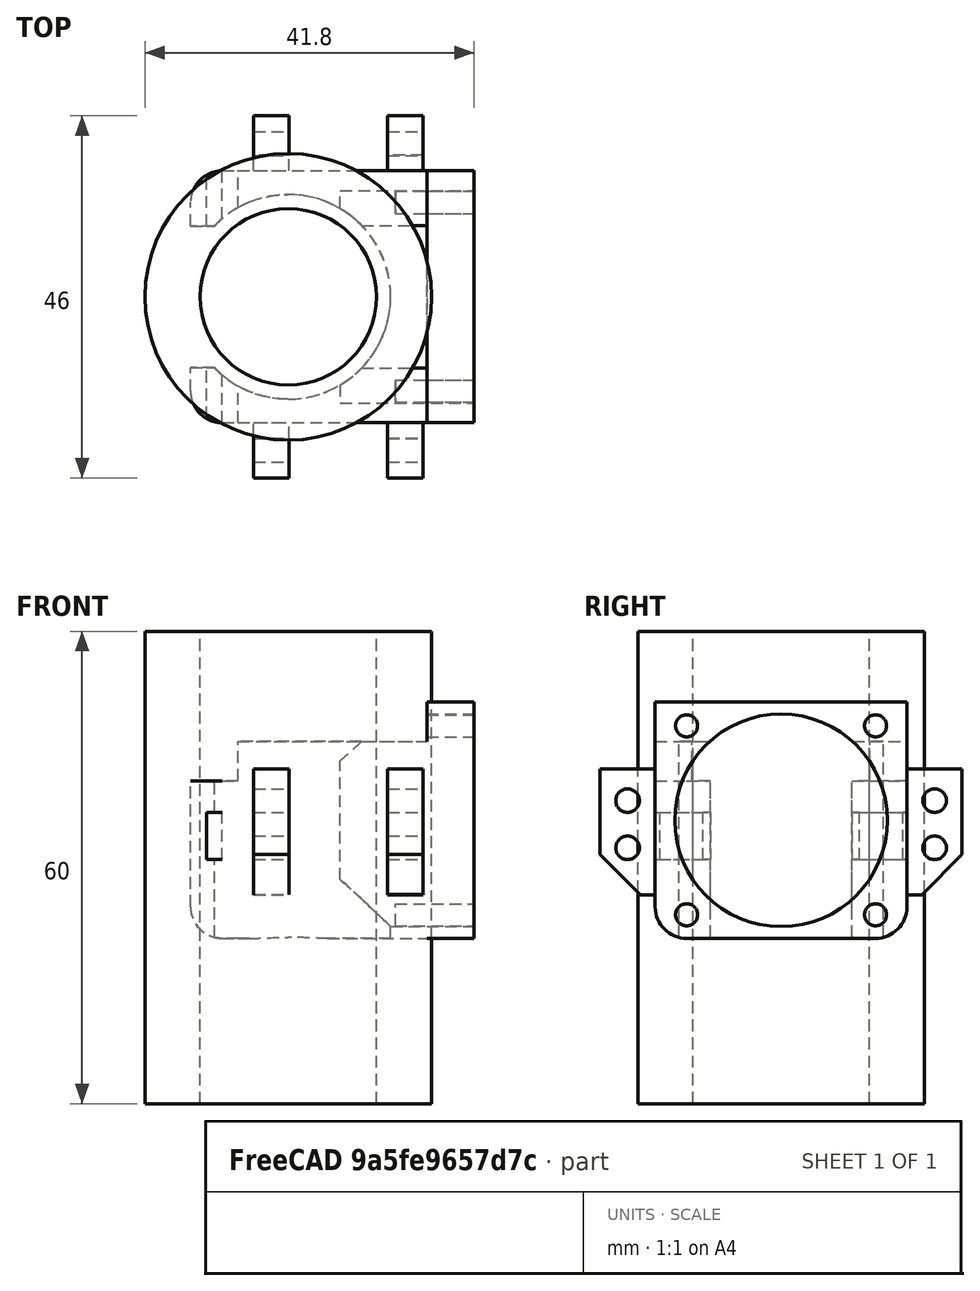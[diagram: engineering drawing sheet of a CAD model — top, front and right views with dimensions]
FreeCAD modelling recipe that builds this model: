
FCSTD DOCUMENT  (FreeCAD 0.15R4671 (Git))
Label: e3dv5
License: All rights reserved
LicenseURL: http://en.wikipedia.org/wiki/All_rights_reserved
objects: Part::Box×13, Part::Cylinder×12, Part::MultiFuse×6, Part::Fillet×4, Part::Cut×3, Mesh::Feature×2, Part::Feature×2
note: 40 computed .brp shape members not serialized (recipe doc carries the construction recipe); baked Part::Feature solids carry a one-line shape summary decoded from their .brp

FEATURE [Part::Box] Box  label="CubeMain"
  Height = 25
  Length = 24
  Width = 32
FEATURE [Part::Box] Box001  label="CubeFrontMask"
  Height = 30
  Length = 6
  Placement = pos=(24,0,0) rot=(0,0,1;0rad)
  Width = 32
FEATURE [Part::Cylinder] Cylinder  label="CylinderHeatSink"
  Angle = 360
  Height = 25
  Placement = pos=(6.4,16,0) rot=(0,0,1;0rad)
  Radius = 13
FEATURE [Part::Cylinder] Cylinder001  label="CylinderFan"
  Angle = 360
  Height = 18
  Placement = pos=(13,16,15) rot=(0,1,0;1.5708rad)
  Radius = 13.5
FEATURE [Part::Cylinder] Cylinder002  label="CylinderBL"
  Angle = 360
  Height = 20
  Placement = pos=(20,4,3) rot=(0,1,0;1.5708rad)
  Radius = 1.4
FEATURE [Part::Cylinder] Cylinder003  label="CylinderTL"
  Angle = 360
  Height = 20
  Placement = pos=(20,4,27) rot=(0,1,0;1.5708rad)
  Radius = 1.4
FEATURE [Part::Cylinder] Cylinder004  label="CylinderTB"
  Angle = 360
  Height = 20
  Placement = pos=(20,28,27) rot=(0,1,0;1.5708rad)
  Radius = 1.4
FEATURE [Part::Cylinder] Cylinder005  label="CylinderRB"
  Angle = 360
  Height = 20
  Placement = pos=(20,28,3) rot=(0,1,0;1.5708rad)
  Radius = 1.4
FEATURE [Part::MultiFuse] Fusion001  label="FusionFanScrews"
  Shapes = -> [Cylinder002,Cylinder003,Cylinder005,Cylinder004]
FEATURE [Part::Box] Box002  label="CubeZipTieL"
  Height = 20
  Length = 6
  Placement = pos=(-6,0,0) rot=(0,0,1;0rad)
  Width = 7
FEATURE [Part::Box] Box003  label="CubZipTieR"
  Height = 20
  Length = 6
  Placement = pos=(-6,25,0) rot=(0,0,1;0rad)
  Width = 7
FEATURE [Part::Box] Box004  label="CubeZipTieHor"
  Height = 6
  Length = 2
  Placement = pos=(-4,0,10) rot=(0,0,1;0rad)
  Width = 32
FEATURE [Part::Cylinder] Cylinder009
  Angle = 360
  Height = 40
  Placement = pos=(0,-3.5,12) rot=(0,1,0;1.5708rad)
  Radius = 1.5
FEATURE [Part::Cylinder] Cylinder010
  Angle = 360
  Height = 40
  Placement = pos=(0,-3.5,6) rot=(0,1,0;1.5708rad)
  Radius = 1.5
FEATURE [Part::Box] Box005  label="Cube005"
  Height = 16
  Length = 4.5
  Placement = pos=(2,-7,0) rot=(0,0,1;0rad)
  Width = 7
FEATURE [Part::Box] Box006  label="Cube006"
  Height = 16
  Length = 4.5
  Placement = pos=(19,-7,0) rot=(0,0,1;0rad)
  Width = 7
FEATURE [Part::Box] Box007  label="Cube007"
  Height = 16
  Length = 4.5
  Placement = pos=(2,32,0) rot=(0,0,1;0rad)
  Width = 7
FEATURE [Part::Box] Box008  label="Cube008"
  Height = 16
  Length = 4.5
  Placement = pos=(19,32,0) rot=(0,0,1;0rad)
  Width = 7
FEATURE [Part::Cylinder] Cylinder011
  Angle = 360
  Height = 40
  Placement = pos=(0,35.5,12) rot=(0,1,0;1.5708rad)
  Radius = 1.5
FEATURE [Part::Cylinder] Cylinder012
  Angle = 360
  Height = 40
  Placement = pos=(0,35.5,6) rot=(0,1,0;1.5708rad)
  Radius = 1.5
FEATURE [Part::MultiFuse] Fusion004  label="FusionWingScrews"
  Placement = pos=(0,0,5.5) rot=(0,0,1;0rad)
  Shapes = -> [Cylinder009,Cylinder010,Cylinder011,Cylinder012]
FEATURE [Part::Box] Box009  label="Cube009"
  Height = 10
  Length = 22
  Placement = pos=(2,-9,-7) rot=(1,0,0;0.785398rad)
  Width = 10
FEATURE [Part::Box] Box010  label="Cube010"
  Height = 10
  Length = 22
  Placement = pos=(2,41,-7) rot=(1,0,0;0.785398rad)
  Width = 10
FEATURE [Part::MultiFuse] Fusion006  label="FusionWings"
  Placement = pos=(0,0,5.5) rot=(0,0,1;0rad)
  Shapes = -> [Box005,Box006,Box007,Box008]
FEATURE [Part::MultiFuse] Fusion005  label="FusionWingCuts"
  Placement = pos=(0,0,5.5) rot=(0,0,1;0rad)
  Shapes = -> [Box009,Box010]
FEATURE [Part::MultiFuse] Fusion  label="FusionCUTS"
  Shapes = -> [Fusion001,Fusion005,Fusion004,Box004,Cylinder,Cylinder001]
FEATURE [Part::MultiFuse] Fusion007  label="FusionMain"
  Shapes = -> [Box,Box002,Fusion006,Box003,Box001]
FEATURE [Part::Fillet] Fillet
  Base = -> Fusion007
  Edges = 1 edges r=4: [Edge86]
FEATURE [Part::Fillet] Fillet001
  Base = -> Fillet
  Edges = 1 edges r=4: [Edge11]
FEATURE [Part::Fillet] Fillet002
  Base = -> Fillet001
  Edges = 1 edges r=4: [Edge66]
FEATURE [Part::Fillet] Fillet003
  Base = -> Fillet002
  Edges = 1 edges r=4: [Edge16]
FEATURE [Part::Cut] Cut  label="CutE3DV5Holder"
  Base = -> Fillet003
  Tool = -> Fusion
FEATURE [Mesh::Feature] E3D_v5_40mm_Duct
FEATURE [Part::Feature] E3D_v5_40mm_Duct001
  Placement = pos=(-37.5,50,14.2) rot=(0,0.965926,-0.258819;3.14159rad)
  shape: large baked B-rep (38 MB .brp); summary skipped
FEATURE [Part::Cylinder] Cylinder014  label="CylinderHeatSinkSignCenter"
  Angle = 360
  Height = 60
  Placement = pos=(6.4,16,-21) rot=(0,0,1;0rad)
  Radius = 11.2
FEATURE [Mesh::Feature] E3D_v5_40mm_Duct_Mirrored
  Placement = pos=(9.5,75,68) rot=(0.694747,-0.694747,-0.186157;3.50969rad)
FEATURE [Part::Feature] E3D_v5_40mm_Duct_Mirrored001
  shape: bbox 45.72 x 69.45 x 41.84 mm, 17238 faces, 0 solids (baked)
FEATURE [Part::Box] Box011  label="Cube"
  Height = 10
  Length = 100
  Placement = pos=(-43,7,-20) rot=(0,0,1;0rad)
  Width = 10
FEATURE [Part::Box] Box012  label="Cube011"
  Height = 10
  Length = 100
  Placement = pos=(-43,15,-20) rot=(0,0,1;0rad)
  Width = 10
FEATURE [Part::Cut] Cut001  label="CutRightFunDuct"
  Base = -> E3D_v5_40mm_Duct001
  Tool = -> Box011
FEATURE [Part::Cut] Cut002  label="CutLeftFunDuct"
  Base = -> E3D_v5_40mm_Duct_Mirrored001
  Tool = -> Box012
FEATURE [Part::Cylinder] Cylinder015  label="CylinderCenter"
  Angle = 360
  Height = 60
  Placement = pos=(6.4,16,-21) rot=(0,0,1;0rad)
  Radius = 18.2
